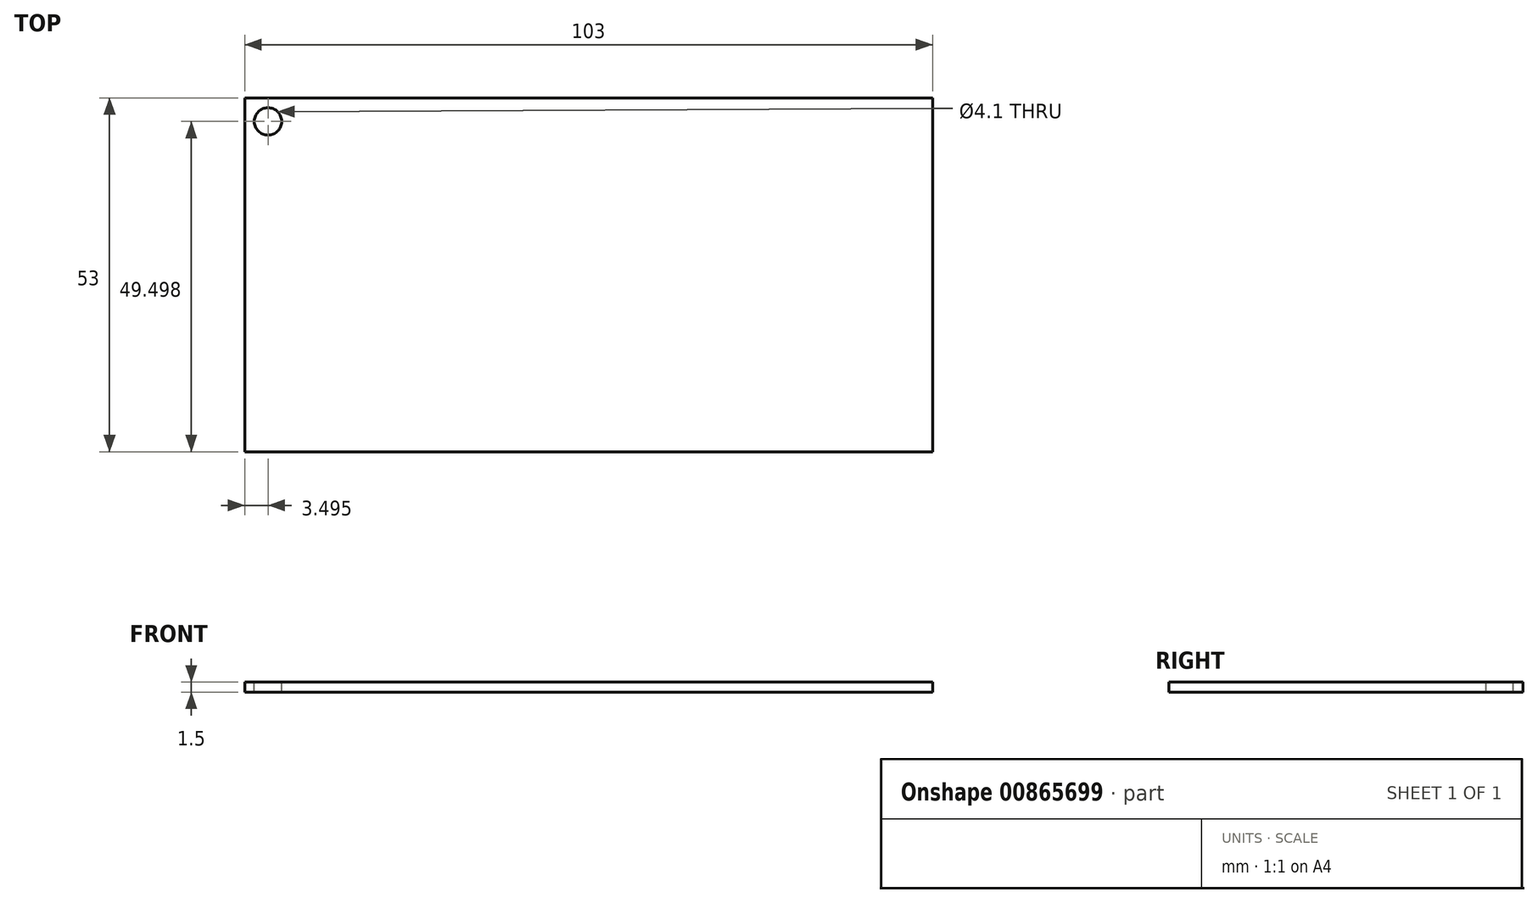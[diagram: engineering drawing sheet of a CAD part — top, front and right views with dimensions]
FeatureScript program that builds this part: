
annotation { "Feature Type Name" : "Feature", "Feature Type Description" : "" }
export const myFeature = defineFeature(function(context is Context, id is Id, definition is map)
    precondition{}
    {
        {
            var Q0;
            Q0=qCreatedBy(makeId("Top.planeOp"),FACE);
            var sketch = newSketch(context, id + "F0", { "sketchPlane" : qUnion([Q0])});
            skLineSegment(sketch, "E0.bottom", {"start": v(-29.76, 25.15) * mm, "end": v(73.24, 25.15) * mm});
            skLineSegment(sketch, "E0.top", {"start": v(-29.76, -27.85) * mm, "end": v(73.24, -27.85) * mm});
            skLineSegment(sketch, "E0.left", {"start": v(-29.76, 25.15) * mm, "end": v(-29.76, -27.85) * mm});
            skLineSegment(sketch, "E0.right", {"start": v(73.24, 25.15) * mm, "end": v(73.24, -27.85) * mm});
            skSolve(sketch);
        }
        {
            var Q0;
            Q0=makeQuery(id+"F0.imprint","IMPRINT",FACE,{"disambiguationData":[TD([[makeQuery(id+"F0.imprint","IMPRINT",EDGE,{"derivedFrom":sQuery(id+"F0.wireOp",EDGE,"E0.bottom")}),-1.0]])]});
            extrude(context, id + "F1", {"entities" : qUnion([Q0]), "depth" : 1.5 * mm, "offsetDistance" : 25.4 * mm});
        }
        {
            var Q0;
            Q0=makeQuery(id+"F1.opExtrude","CAP_FACE",FACE,{"disambiguationData":[OSD([sQuery(id+"F0.wireOp",EDGE,"E0.bottom"),sQuery(id+"F0.wireOp",EDGE,"E0.top"),sQuery(id+"F0.wireOp",EDGE,"E0.left"),sQuery(id+"F0.wireOp",EDGE,"E0.right")])],"isStart":false});
            var sketch = newSketch(context, id + "F2", { "sketchPlane" : qUnion([Q0])});
            skCircle(sketch, "E1", {"center": v(-26.26, 21.65) * mm, "radius": 2 * mm});
            skSolve(sketch);
        }
        {
            var Q0;
            Q0=sQuery(id+"F2.wireOp",VERTEX,"E1.center");
            var Q1;
            Q1=makeQuery(id+"F1.opExtrude","SWEPT_BODY",BODY,{"disambiguationData":[OSD([sQuery(id+"F0.wireOp",EDGE,"E0.bottom"),sQuery(id+"F0.wireOp",EDGE,"E0.top"),sQuery(id+"F0.wireOp",EDGE,"E0.left"),sQuery(id+"F0.wireOp",EDGE,"E0.right")])]});
            hole(context, id + "F3", {"style" : HoleStyle.SIMPLE, "endStyle" : HoleEndStyle.THROUGH, "standardTappedOrClearance" : lookupTablePath({ "standard" : "ISO", "engagement" : "75%", "pitch" : "0.9 mm", "size" : "M5", "type" : "Tapped" }), "standardBlindInLast" : lookupTablePath({ "standard" : "ISO", "engagement" : "75%", "pitch" : "0.9 mm", "size" : "M5", "type" : "Tapped" }), "holeDiameter" : 4.1 * mm, "majorDiameter" : 6.35 * mm, "showTappedDepth" : true, "isTappedThrough" : true, "tappedDepth" : 12.7 * mm, "tapClearance" : 3, "locations" : qUnion([Q0]), "scope" : qUnion([Q1])});
        }
    });
